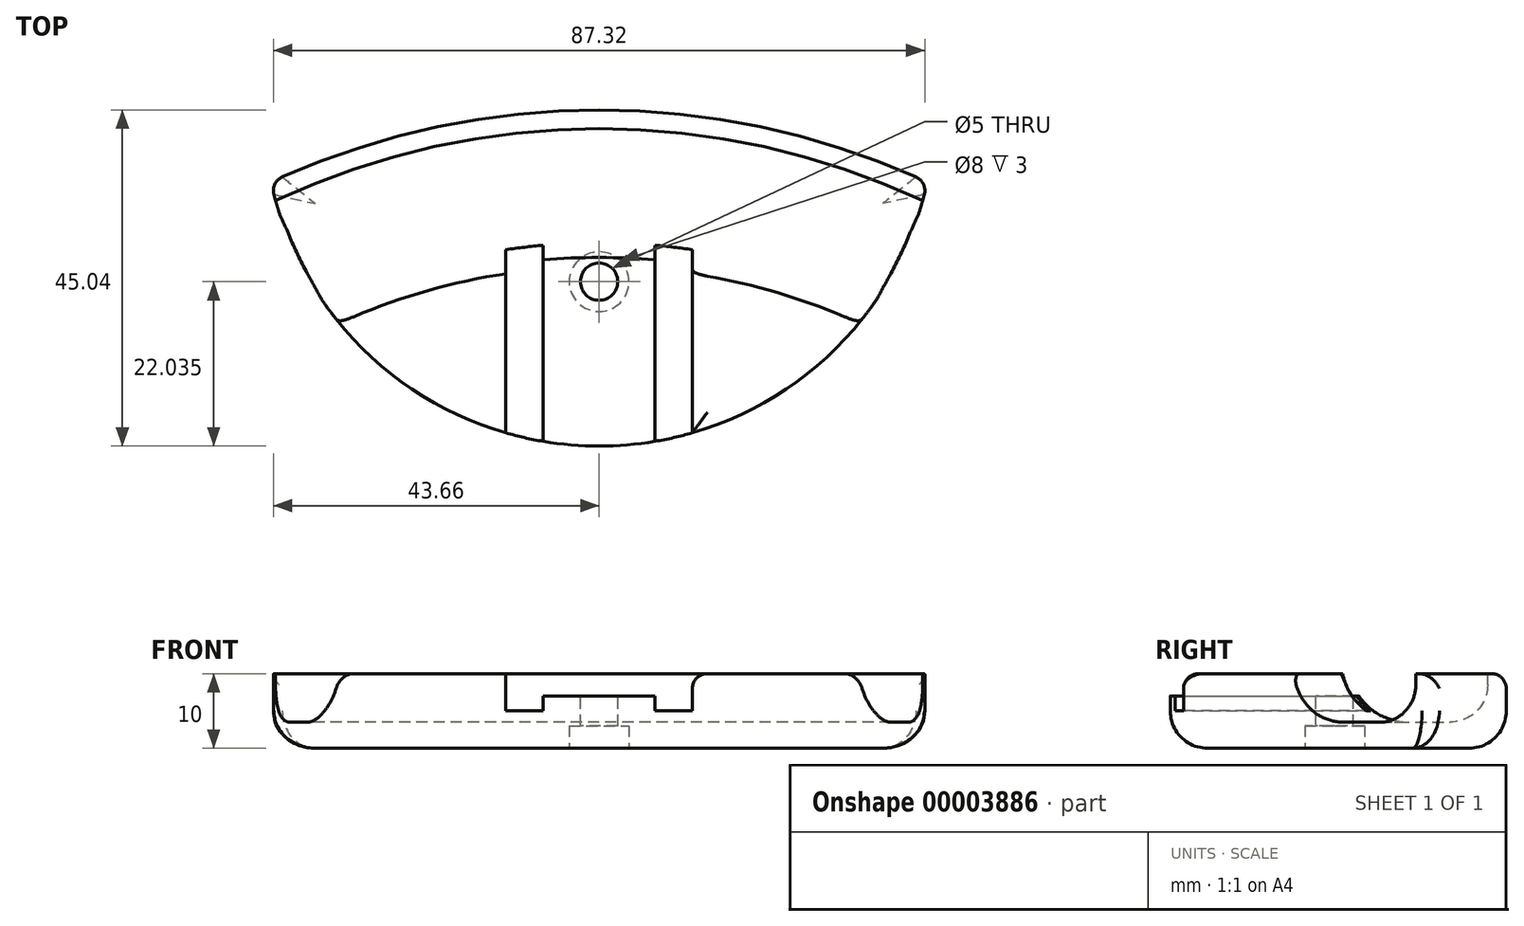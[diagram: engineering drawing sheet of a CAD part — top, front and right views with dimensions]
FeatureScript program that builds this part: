
annotation { "Feature Type Name" : "Feature", "Feature Type Description" : "" }
export const myFeature = defineFeature(function(context is Context, id is Id, definition is map)
    precondition{}
    {
        {
            var Q0;
            Q0=qCreatedBy(makeId("Top.planeOp"),FACE);
            var sketch = newSketch(context, id + "F0", { "sketchPlane" : qUnion([Q0])});
            skLineSegment(sketch, "E0.bottom", {"start": v(-12.5, 20) * mm, "end": v(12.5, 20) * mm});
            skLineSegment(sketch, "E0.top", {"start": v(-12.5, -20) * mm, "end": v(12.5, -20) * mm});
            skLineSegment(sketch, "E0.left", {"start": v(-12.5, 20) * mm, "end": v(-12.5, -20) * mm});
            skLineSegment(sketch, "E0.right", {"start": v(12.5, 20) * mm, "end": v(12.5, -20) * mm});
            skArc(sketch, "E1", {"start": v(43.99, 13.6) * mm, "mid": v(0, 23.27) * mm, "end": v(-43.99, 13.6) * mm});
            skArc(sketch, "E2", {"start": v(-43.99, 13.6) * mm, "mid": v(0, -21.77) * mm, "end": v(43.99, 13.6) * mm});
            skPoint(sketch, "E3", {"position": v(-43.99, 13.6) * mm});
            skPoint(sketch, "E4", {"position": v(43.99, 13.6) * mm});
            skPoint(sketch, "E5", {"position": v(-43.37, 11.14) * mm});
            skPoint(sketch, "E6", {"position": v(43.37, 11.14) * mm});
            skArc(sketch, "E7.trimOffspring", {"start": v(43.37, 11.14) * mm, "mid": v(0, 20.77) * mm, "end": v(-43.37, 11.14) * mm});
            skLineSegment(sketch, "E8", {"start": v(0, 20) * mm, "end": v(0, -20) * mm, "construction": true});
            skArc(sketch, "E9", {"start": v(34.82, -5.3) * mm, "mid": v(0, 2.27) * mm, "end": v(-34.82, -5.3) * mm});
            skPoint(sketch, "E10", {"position": v(0, 0.27) * mm});
            skCircle(sketch, "E11", {"center": v(0, 0.27) * mm, "radius": 2.5 * mm});
            skLineSegment(sketch, "E12", {"start": v(-7.5, -12.17) * mm, "end": v(7.5, -12.17) * mm, "construction": true});
            skPoint(sketch, "E13", {"position": v(0, -12.17) * mm});
            skLineSegment(sketch, "E14", {"start": v(-7.5, -21.14) * mm, "end": v(-7.5, 10.15) * mm});
            skLineSegment(sketch, "E15", {"start": v(7.5, -21.14) * mm, "end": v(7.5, 10.15) * mm});
            skLineSegment(sketch, "E16", {"start": v(-7.5, 10.15) * mm, "end": v(7.5, 10.15) * mm});
            skSolve(sketch);
        }
        {
            var Q0;
            Q0=makeQuery(id+"F0.imprint","IMPRINT",FACE,{"disambiguationData":[TD([[makeQuery(id+"F0.imprint","IMPRINT",EDGE,{"derivedFrom":sQuery(id+"F0.wireOp",EDGE,"E1")}),1.0]])]});
            var Q1;
            {var subQ1=sQuery(id+"F0.wireOp",EDGE,"E7.trimOffspring");Q1=makeQuery(id+"F0.imprint","IMPRINT",FACE,{"disambiguationData":[TD([[makeQuery(id+"F0.imprint","IMPRINT",EDGE,{"derivedFrom":subQ1}),1.0]])]});}
            var Q2;
            {var subQ0=sQuery(id+"F0.wireOp",EDGE,"E9");Q2=makeQuery(id+"F0.imprint","IMPRINT",FACE,{"disambiguationData":[TD([[makeQuery(id+"F0.imprint","IMPRINT",EDGE,{"derivedFrom":subQ0}),1.0]])]});}
            var Q3;
            {var subQ5=sQuery(id+"F0.wireOp",EDGE,"E0.top");Q3=makeQuery(id+"F0.imprint","IMPRINT",FACE,{"disambiguationData":[TD([[makeQuery(id+"F0.imprint","IMPRINT",EDGE,{"derivedFrom":subQ5}),1.0]])]});}
            var Q4;
            {var subQ1=sQuery(id+"F0.wireOp",EDGE,"E0.top");Q4=makeQuery(id+"F0.imprint","IMPRINT",FACE,{"disambiguationData":[TD([[makeQuery(id+"F0.imprint","IMPRINT",EDGE,{"derivedFrom":subQ1}),-1.0]])]});}
            var Q5;
            {var subQ3=sQuery(id+"F0.wireOp",EDGE,"E2");var subQ5=sQuery(id+"F0.wireOp",EDGE,"E7.trimOffspring");var subQ6=makeQuery(id+"F0.imprint","INTERSECT",VERTEX,{"disambiguationData":[OD(0.0)],"derivedFrom":[subQ3,subQ5]});Q5=makeQuery(id+"F0.imprint","IMPRINT",FACE,{"disambiguationData":[TD([[makeQuery(id+"F0.imprint","IMPRINT",EDGE,{"disambiguationData":[TD([[subQ6,1.0]])],"derivedFrom":subQ3}),1.0]])]});}
            var Q6;
            {var subQ5=sQuery(id+"F0.wireOp",EDGE,"E0.bottom");Q6=makeQuery(id+"F0.imprint","IMPRINT",FACE,{"disambiguationData":[TD([[makeQuery(id+"F0.imprint","IMPRINT",EDGE,{"derivedFrom":subQ5}),-1.0]])]});}
            var Q7;
            {var subQ3=sQuery(id+"F0.wireOp",EDGE,"E2");var subQ5=sQuery(id+"F0.wireOp",EDGE,"E7.trimOffspring");var subQ6=makeQuery(id+"F0.imprint","INTERSECT",VERTEX,{"disambiguationData":[OD(1.0)],"derivedFrom":[subQ3,subQ5]});Q7=makeQuery(id+"F0.imprint","IMPRINT",FACE,{"disambiguationData":[TD([[makeQuery(id+"F0.imprint","IMPRINT",EDGE,{"disambiguationData":[TD([[subQ6,-1.0]])],"derivedFrom":subQ3}),1.0]])]});}
            var Q8;
            {var subQ0=sQuery(id+"F0.wireOp",EDGE,"E11");var subQ1=sQuery(id+"F0.wireOp",EDGE,"E9");var subQ3=makeQuery(id+"F0.imprint","INTERSECT",VERTEX,{"disambiguationData":[OD(0.0)],"derivedFrom":[subQ1,subQ0]});Q8=makeQuery(id+"F0.imprint","IMPRINT",FACE,{"disambiguationData":[TD([[makeQuery(id+"F0.imprint","IMPRINT",EDGE,{"disambiguationData":[TD([[subQ3,-1.0]])],"derivedFrom":subQ1}),-1.0]])]});}
            var Q9;
            {var subQ0=sQuery(id+"F0.wireOp",EDGE,"E11");var subQ1=sQuery(id+"F0.wireOp",EDGE,"E9");var subQ3=makeQuery(id+"F0.imprint","INTERSECT",VERTEX,{"disambiguationData":[OD(0.0)],"derivedFrom":[subQ1,subQ0]});Q9=makeQuery(id+"F0.imprint","IMPRINT",FACE,{"disambiguationData":[TD([[makeQuery(id+"F0.imprint","IMPRINT",EDGE,{"disambiguationData":[TD([[subQ3,-1.0]])],"derivedFrom":subQ1}),1.0]])]});}
            var Q10;
            {var subQ0=sQuery(id+"F0.wireOp",EDGE,"E9");var subQ3=sQuery(id+"F0.wireOp",EDGE,"E2");var subQ4=makeQuery(id+"F0.imprint","INTERSECT",VERTEX,{"disambiguationData":[OD(1.0)],"derivedFrom":[subQ3,subQ0]});Q10=makeQuery(id+"F0.imprint","IMPRINT",FACE,{"disambiguationData":[TD([[makeQuery(id+"F0.imprint","IMPRINT",EDGE,{"disambiguationData":[TD([[subQ4,1.0]])],"derivedFrom":subQ0}),1.0]])]});}
            var Q11;
            {var subQ0=sQuery(id+"F0.wireOp",EDGE,"E9");var subQ3=sQuery(id+"F0.wireOp",EDGE,"E2");var subQ4=makeQuery(id+"F0.imprint","INTERSECT",VERTEX,{"disambiguationData":[OD(0.0)],"derivedFrom":[subQ3,subQ0]});Q11=makeQuery(id+"F0.imprint","IMPRINT",FACE,{"disambiguationData":[TD([[makeQuery(id+"F0.imprint","IMPRINT",EDGE,{"disambiguationData":[TD([[subQ4,-1.0]])],"derivedFrom":subQ0}),1.0]])]});}
            var Q12;
            {var subQ4=sQuery(id+"F0.wireOp",EDGE,"f2ed5ddf-1e71-4b46-be9b-5d21263913f5.bottom");Q12=makeQuery(id+"F0.imprint","IMPRINT",FACE,{"disambiguationData":[TD([[makeQuery(id+"F0.imprint","IMPRINT",EDGE,{"derivedFrom":subQ4}),-1.0]])]});}
            var Q13;
            {var subQ0=sQuery(id+"F0.wireOp",EDGE,"f2ed5ddf-1e71-4b46-be9b-5d21263913f5.top");Q13=makeQuery(id+"F0.imprint","IMPRINT",FACE,{"disambiguationData":[TD([[makeQuery(id+"F0.imprint","IMPRINT",EDGE,{"derivedFrom":subQ0}),1.0]])]});}
            var Q14;
            {var subQ1=sQuery(id+"F0.wireOp",EDGE,"E0.bottom");var subQ5=sQuery(id+"F0.wireOp",EDGE,"E14");var subQ6=makeQuery(id+"F0.imprint","INTERSECT",VERTEX,{"derivedFrom":[subQ1,subQ5]});Q14=makeQuery(id+"F0.imprint","IMPRINT",FACE,{"disambiguationData":[TD([[makeQuery(id+"F0.imprint","IMPRINT",EDGE,{"disambiguationData":[TD([[subQ6,-1.0]])],"derivedFrom":subQ1}),1.0]])]});}
            var Q15;
            {var subQ3=sQuery(id+"F0.wireOp",EDGE,"E0.bottom");var subQ8=sQuery(id+"F0.wireOp",EDGE,"E14");var subQ10=makeQuery(id+"F0.imprint","INTERSECT",VERTEX,{"derivedFrom":[subQ3,subQ8]});Q15=makeQuery(id+"F0.imprint","IMPRINT",FACE,{"disambiguationData":[TD([[makeQuery(id+"F0.imprint","IMPRINT",EDGE,{"disambiguationData":[TD([[subQ10,-1.0]])],"derivedFrom":subQ3}),-1.0]])]});}
            var Q16;
            {var subQ3=sQuery(id+"F0.wireOp",EDGE,"E0.top");var subQ5=sQuery(id+"F0.wireOp",EDGE,"E14");var subQ7=makeQuery(id+"F0.imprint","INTERSECT",VERTEX,{"derivedFrom":[subQ3,subQ5]});Q16=makeQuery(id+"F0.imprint","IMPRINT",FACE,{"disambiguationData":[TD([[makeQuery(id+"F0.imprint","IMPRINT",EDGE,{"disambiguationData":[TD([[subQ7,-1.0]])],"derivedFrom":subQ3}),1.0]])]});}
            var Q17;
            {var subQ0=sQuery(id+"F0.wireOp",EDGE,"E14");var subQ1=sQuery(id+"F0.wireOp",EDGE,"E0.top");var subQ2=makeQuery(id+"F0.imprint","INTERSECT",VERTEX,{"derivedFrom":[subQ1,subQ0]});Q17=makeQuery(id+"F0.imprint","IMPRINT",FACE,{"disambiguationData":[TD([[makeQuery(id+"F0.imprint","IMPRINT",EDGE,{"disambiguationData":[TD([[subQ2,-1.0]])],"derivedFrom":subQ1}),-1.0]])]});}
            var Q18;
            {var subQ3=sQuery(id+"F0.wireOp",EDGE,"E16");Q18=makeQuery(id+"F0.imprint","IMPRINT",FACE,{"disambiguationData":[TD([[makeQuery(id+"F0.imprint","IMPRINT",EDGE,{"derivedFrom":subQ3}),-1.0]])]});}
            extrude(context, id + "F1", {"entities" : qUnion([Q0, Q1, Q2, Q3, Q4, Q5, Q6, Q7, Q8, Q9, Q10, Q11, Q12, Q13, Q14, Q15, Q16, Q17, Q18]), "oppositeDirection" : true, "depth" : 10 * mm});
        }
        {
            var Q0;
            {var subQ1=sQuery(id+"F0.wireOp",EDGE,"E7.trimOffspring");Q0=makeQuery(id+"F0.imprint","IMPRINT",FACE,{"disambiguationData":[TD([[makeQuery(id+"F0.imprint","IMPRINT",EDGE,{"derivedFrom":subQ1}),1.0]])]});}
            var Q1;
            {var subQ3=sQuery(id+"F0.wireOp",EDGE,"E2");var subQ5=sQuery(id+"F0.wireOp",EDGE,"E7.trimOffspring");var subQ6=makeQuery(id+"F0.imprint","INTERSECT",VERTEX,{"disambiguationData":[OD(0.0)],"derivedFrom":[subQ3,subQ5]});Q1=makeQuery(id+"F0.imprint","IMPRINT",FACE,{"disambiguationData":[TD([[makeQuery(id+"F0.imprint","IMPRINT",EDGE,{"disambiguationData":[TD([[subQ6,1.0]])],"derivedFrom":subQ3}),1.0]])]});}
            var Q2;
            {var subQ5=sQuery(id+"F0.wireOp",EDGE,"E0.bottom");Q2=makeQuery(id+"F0.imprint","IMPRINT",FACE,{"disambiguationData":[TD([[makeQuery(id+"F0.imprint","IMPRINT",EDGE,{"derivedFrom":subQ5}),-1.0]])]});}
            var Q3;
            {var subQ3=sQuery(id+"F0.wireOp",EDGE,"E2");var subQ5=sQuery(id+"F0.wireOp",EDGE,"E7.trimOffspring");var subQ6=makeQuery(id+"F0.imprint","INTERSECT",VERTEX,{"disambiguationData":[OD(1.0)],"derivedFrom":[subQ3,subQ5]});Q3=makeQuery(id+"F0.imprint","IMPRINT",FACE,{"disambiguationData":[TD([[makeQuery(id+"F0.imprint","IMPRINT",EDGE,{"disambiguationData":[TD([[subQ6,-1.0]])],"derivedFrom":subQ3}),1.0]])]});}
            var Q4;
            {var subQ4=sQuery(id+"F0.wireOp",EDGE,"f2ed5ddf-1e71-4b46-be9b-5d21263913f5.bottom");Q4=makeQuery(id+"F0.imprint","IMPRINT",FACE,{"disambiguationData":[TD([[makeQuery(id+"F0.imprint","IMPRINT",EDGE,{"derivedFrom":subQ4}),-1.0]])]});}
            var Q5;
            {var subQ0=sQuery(id+"F0.wireOp",EDGE,"E11");var subQ1=sQuery(id+"F0.wireOp",EDGE,"E9");var subQ3=makeQuery(id+"F0.imprint","INTERSECT",VERTEX,{"disambiguationData":[OD(0.0)],"derivedFrom":[subQ1,subQ0]});Q5=makeQuery(id+"F0.imprint","IMPRINT",FACE,{"disambiguationData":[TD([[makeQuery(id+"F0.imprint","IMPRINT",EDGE,{"disambiguationData":[TD([[subQ3,-1.0]])],"derivedFrom":subQ1}),-1.0]])]});}
            var Q6;
            {var subQ3=sQuery(id+"F0.wireOp",EDGE,"E0.bottom");var subQ8=sQuery(id+"F0.wireOp",EDGE,"E14");var subQ10=makeQuery(id+"F0.imprint","INTERSECT",VERTEX,{"derivedFrom":[subQ3,subQ8]});Q6=makeQuery(id+"F0.imprint","IMPRINT",FACE,{"disambiguationData":[TD([[makeQuery(id+"F0.imprint","IMPRINT",EDGE,{"disambiguationData":[TD([[subQ10,-1.0]])],"derivedFrom":subQ3}),-1.0]])]});}
            var Q7;
            {var subQ3=sQuery(id+"F0.wireOp",EDGE,"E16");Q7=makeQuery(id+"F0.imprint","IMPRINT",FACE,{"disambiguationData":[TD([[makeQuery(id+"F0.imprint","IMPRINT",EDGE,{"derivedFrom":subQ3}),-1.0]])]});}
            extrude(context, id + "F2", {"entities" : qUnion([Q0, Q1, Q2, Q3, Q4, Q5, Q6, Q7]), "operationType" : NewBodyOperationType.REMOVE, "oppositeDirection" : true, "depth" : 6.5 * mm});
        }
        {
            var Q0;
            {var subQ5=sQuery(id+"F0.wireOp",EDGE,"E0.top");Q0=makeQuery(id+"F0.imprint","IMPRINT",FACE,{"disambiguationData":[TD([[makeQuery(id+"F0.imprint","IMPRINT",EDGE,{"derivedFrom":subQ5}),1.0]])]});}
            var Q1;
            {var subQ1=sQuery(id+"F0.wireOp",EDGE,"E0.top");Q1=makeQuery(id+"F0.imprint","IMPRINT",FACE,{"disambiguationData":[TD([[makeQuery(id+"F0.imprint","IMPRINT",EDGE,{"derivedFrom":subQ1}),-1.0]])]});}
            var Q2;
            {var subQ0=sQuery(id+"F0.wireOp",EDGE,"f2ed5ddf-1e71-4b46-be9b-5d21263913f5.top");Q2=makeQuery(id+"F0.imprint","IMPRINT",FACE,{"disambiguationData":[TD([[makeQuery(id+"F0.imprint","IMPRINT",EDGE,{"derivedFrom":subQ0}),1.0]])]});}
            var Q3;
            {var subQ0=sQuery(id+"F0.wireOp",EDGE,"E11");var subQ1=sQuery(id+"F0.wireOp",EDGE,"E9");var subQ3=makeQuery(id+"F0.imprint","INTERSECT",VERTEX,{"disambiguationData":[OD(0.0)],"derivedFrom":[subQ1,subQ0]});Q3=makeQuery(id+"F0.imprint","IMPRINT",FACE,{"disambiguationData":[TD([[makeQuery(id+"F0.imprint","IMPRINT",EDGE,{"disambiguationData":[TD([[subQ3,-1.0]])],"derivedFrom":subQ1}),1.0]])]});}
            extrude(context, id + "F3", {"entities" : qUnion([Q0, Q1, Q2, Q3]), "operationType" : NewBodyOperationType.REMOVE, "oppositeDirection" : true, "depth" : 5 * mm});
        }
        {
            var Q0;
            {var subQ0=sQuery(id+"F0.wireOp",EDGE,"E9");var subQ1=sQuery(id+"F0.wireOp",EDGE,"E0.right");Q0=makeQuery(id+"F3.boolean.opBoolean","SPLIT",EDGE,{"disambiguationData":[TD([makeQuery(id+"F3.opExtrude","SWEPT_FACE",FACE,{"disambiguationData":[OSD([subQ1])]})])],"derivedFrom":makeQuery(id+"F2.boolean.opBoolean","COPY",EDGE,{"derivedFrom":makeQuery(id+"F2.opExtrude","CAP_EDGE",EDGE,{"disambiguationData":[OSD([subQ0])],"isStart":false})})});}
            var Q1;
            {var subQ0=sQuery(id+"F0.wireOp",EDGE,"E9");var subQ2=sQuery(id+"F0.wireOp",EDGE,"E0.left");Q1=makeQuery(id+"F3.boolean.opBoolean","SPLIT",EDGE,{"disambiguationData":[TD([makeQuery(id+"F3.opExtrude","SWEPT_FACE",FACE,{"disambiguationData":[OSD([subQ2])]})])],"derivedFrom":makeQuery(id+"F2.boolean.opBoolean","COPY",EDGE,{"derivedFrom":makeQuery(id+"F2.opExtrude","CAP_EDGE",EDGE,{"disambiguationData":[OSD([subQ0])],"isStart":false})})});}
            fillet(context, id + "F4", {"entities" : qUnion([Q0, Q1]), "radius" : 8 * mm, "tangentPropagation" : true, "allowEdgeOverflow" : false});
        }
        {
            var Q0;
            Q0=makeQuery(id+"F1.opExtrude","CAP_EDGE",EDGE,{"disambiguationData":[OSD([sQuery(id+"F0.wireOp",EDGE,"E2")])],"isStart":false});
            var Q1;
            Q1=makeQuery(id+"F1.opExtrude","CAP_EDGE",EDGE,{"disambiguationData":[OSD([sQuery(id+"F0.wireOp",EDGE,"E1")])],"isStart":false});
            fillet(context, id + "F5", {"entities" : qUnion([Q0, Q1]), "radius" : 5 * mm, "tangentPropagation" : true, "allowEdgeOverflow" : false});
        }
        {
            var Q0;
            Q0=makeQuery(id+"F1.opExtrude","CAP_EDGE",EDGE,{"disambiguationData":[OSD([sQuery(id+"F0.wireOp",EDGE,"E1")])],"isStart":true});
            var Q1;
            {var subQ0=sQuery(id+"F0.wireOp",EDGE,"E2");var subQ1=makeQuery(id+"F2.opExtrude","SWEPT_FACE",FACE,{"disambiguationData":[OSD([sQuery(id+"F0.wireOp",EDGE,"E9")])]});var subQ2=makeQuery(id+"F1.opExtrude","SWEPT_FACE",FACE,{"disambiguationData":[OSD([subQ0])]});var subQ3=makeQuery(id+"F1.opExtrude","CAP_FACE",FACE,{"disambiguationData":[OSD([sQuery(id+"F0.wireOp",EDGE,"E1"),subQ0])],"isStart":true});Q1=makeQuery(id+"F3.boolean.opBoolean","SPLIT",EDGE,{"disambiguationData":[TD([makeQuery(id+"F3.opExtrude","SWEPT_FACE",FACE,{"disambiguationData":[OSD([sQuery(id+"F0.wireOp",EDGE,"E0.left")])]})])],"derivedFrom":makeQuery(id+"F2.boolean.opBoolean","SPLIT",EDGE,{"disambiguationData":[TD([subQ3,subQ2,subQ1])],"derivedFrom":makeQuery(id+"F1.opExtrude","CAP_EDGE",EDGE,{"disambiguationData":[OSD([subQ0])],"isStart":true})})});}
            var Q2;
            {var subQ0=sQuery(id+"F0.wireOp",EDGE,"E2");var subQ1=makeQuery(id+"F2.opExtrude","SWEPT_FACE",FACE,{"disambiguationData":[OSD([sQuery(id+"F0.wireOp",EDGE,"E9")])]});var subQ2=makeQuery(id+"F1.opExtrude","SWEPT_FACE",FACE,{"disambiguationData":[OSD([subQ0])]});var subQ3=makeQuery(id+"F1.opExtrude","CAP_FACE",FACE,{"disambiguationData":[OSD([sQuery(id+"F0.wireOp",EDGE,"E1"),subQ0])],"isStart":true});Q2=makeQuery(id+"F3.boolean.opBoolean","SPLIT",EDGE,{"disambiguationData":[TD([makeQuery(id+"F3.opExtrude","SWEPT_FACE",FACE,{"disambiguationData":[OSD([sQuery(id+"F0.wireOp",EDGE,"E0.right")])]})])],"derivedFrom":makeQuery(id+"F2.boolean.opBoolean","SPLIT",EDGE,{"disambiguationData":[TD([subQ3,subQ2,subQ1])],"derivedFrom":makeQuery(id+"F1.opExtrude","CAP_EDGE",EDGE,{"disambiguationData":[OSD([subQ0])],"isStart":true})})});}
            var Q3;
            Q3=makeQuery(id+"F3.boolean.opBoolean","COPY",EDGE,{"derivedFrom":makeQuery(id+"F3.opExtrude","SWEPT_EDGE",EDGE,{"disambiguationData":[OSD([sQuery(id+"F0.wireOp",EDGE,"E0.top"),sQuery(id+"F0.wireOp",EDGE,"E0.right"),sQuery(id+"F0.wireOp",EDGE,"E2")])]})});
            var Q4;
            Q4=makeQuery(id+"F3.boolean.opBoolean","COPY",EDGE,{"derivedFrom":makeQuery(id+"F3.opExtrude","SWEPT_EDGE",EDGE,{"disambiguationData":[OSD([sQuery(id+"F0.wireOp",EDGE,"E0.top"),sQuery(id+"F0.wireOp",EDGE,"E0.left"),sQuery(id+"F0.wireOp",EDGE,"E2")])]})});
            var Q5;
            Q5=makeQuery(id+"F3.boolean.opBoolean","COPY",EDGE,{"derivedFrom":makeQuery(id+"F3.opExtrude","CAP_EDGE",EDGE,{"disambiguationData":[OSD([sQuery(id+"F0.wireOp",EDGE,"E0.left")])],"isStart":true})});
            var Q6;
            Q6=makeQuery(id+"F3.boolean.opBoolean","COPY",EDGE,{"derivedFrom":makeQuery(id+"F3.opExtrude","CAP_EDGE",EDGE,{"disambiguationData":[OSD([sQuery(id+"F0.wireOp",EDGE,"E0.right")])],"isStart":true})});
            var Q7;
            {var subQ0=sQuery(id+"F0.wireOp",EDGE,"E9");Q7=makeQuery(id+"F3.boolean.opBoolean","SPLIT",EDGE,{"disambiguationData":[TD([makeQuery(id+"F3.opExtrude","SWEPT_FACE",FACE,{"disambiguationData":[OSD([sQuery(id+"F0.wireOp",EDGE,"E0.left")])]})])],"derivedFrom":makeQuery(id+"F2.boolean.opBoolean","COPY",EDGE,{"derivedFrom":makeQuery(id+"F2.opExtrude","CAP_EDGE",EDGE,{"disambiguationData":[OSD([subQ0])],"isStart":true})})});}
            var Q8;
            {var subQ0=sQuery(id+"F0.wireOp",EDGE,"E9");Q8=makeQuery(id+"F3.boolean.opBoolean","SPLIT",EDGE,{"disambiguationData":[TD([makeQuery(id+"F3.opExtrude","SWEPT_FACE",FACE,{"disambiguationData":[OSD([sQuery(id+"F0.wireOp",EDGE,"E0.right")])]})])],"derivedFrom":makeQuery(id+"F2.boolean.opBoolean","COPY",EDGE,{"derivedFrom":makeQuery(id+"F2.opExtrude","CAP_EDGE",EDGE,{"disambiguationData":[OSD([subQ0])],"isStart":true})})});}
            var Q9;
            Q9=makeQuery(id+"F2.boolean.opBoolean","COPY",EDGE,{"derivedFrom":makeQuery(id+"F2.opExtrude","CAP_EDGE",EDGE,{"disambiguationData":[OSD([sQuery(id+"F0.wireOp",EDGE,"E7.trimOffspring")])],"isStart":true})});
            var Q10;
            {var subQ0=sQuery(id+"F0.wireOp",EDGE,"E1");var subQ1=sQuery(id+"F0.wireOp",EDGE,"E2");Q10=makeQuery(id+"F1.opExtrude","SWEPT_EDGE",EDGE,{"disambiguationData":[OSD([subQ0,subQ1]),TDD([makeQuery(id+"F0.imprint","INTERSECT",VERTEX,{"disambiguationData":[OD(1.0)],"derivedFrom":[subQ0,subQ1]})])]});}
            var Q11;
            {var subQ0=sQuery(id+"F0.wireOp",EDGE,"E1");var subQ1=sQuery(id+"F0.wireOp",EDGE,"E2");Q11=makeQuery(id+"F1.opExtrude","SWEPT_EDGE",EDGE,{"disambiguationData":[OSD([subQ0,subQ1]),TDD([makeQuery(id+"F0.imprint","INTERSECT",VERTEX,{"disambiguationData":[OD(0.0)],"derivedFrom":[subQ0,subQ1]})])]});}
            fillet(context, id + "F6", {"entities" : qUnion([Q0, Q1, Q2, Q3, Q4, Q5, Q6, Q7, Q8, Q9, Q10, Q11]), "radius" : 2 * mm, "tangentPropagation" : true, "allowEdgeOverflow" : false});
        }
        {
            var Q0;
            Q0=makeQuery(id+"F2.boolean.opBoolean","COPY",EDGE,{"derivedFrom":makeQuery(id+"F2.opExtrude","CAP_EDGE",EDGE,{"disambiguationData":[OSD([sQuery(id+"F0.wireOp",EDGE,"E7.trimOffspring")])],"isStart":false})});
            fillet(context, id + "F7", {"entities" : qUnion([Q0]), "radius" : 5 * mm, "tangentPropagation" : true, "allowEdgeOverflow" : false});
        }
        {
            var Q0;
            {var subQ0=sQuery(id+"F0.wireOp",EDGE,"E11");var subQ1=sQuery(id+"F0.wireOp",EDGE,"E9");var subQ3=makeQuery(id+"F0.imprint","INTERSECT",VERTEX,{"disambiguationData":[OD(0.0)],"derivedFrom":[subQ1,subQ0]});Q0=makeQuery(id+"F0.imprint","IMPRINT",FACE,{"disambiguationData":[TD([[makeQuery(id+"F0.imprint","IMPRINT",EDGE,{"disambiguationData":[TD([[subQ3,-1.0]])],"derivedFrom":subQ1}),-1.0]])]});}
            var Q1;
            {var subQ0=sQuery(id+"F0.wireOp",EDGE,"E11");var subQ1=sQuery(id+"F0.wireOp",EDGE,"E9");var subQ3=makeQuery(id+"F0.imprint","INTERSECT",VERTEX,{"disambiguationData":[OD(0.0)],"derivedFrom":[subQ1,subQ0]});Q1=makeQuery(id+"F0.imprint","IMPRINT",FACE,{"disambiguationData":[TD([[makeQuery(id+"F0.imprint","IMPRINT",EDGE,{"disambiguationData":[TD([[subQ3,-1.0]])],"derivedFrom":subQ1}),1.0]])]});}
            extrude(context, id + "F8", {"entities" : qUnion([Q0, Q1]), "operationType" : NewBodyOperationType.REMOVE, "endBound" : BoundingType.THROUGH_ALL, "oppositeDirection" : true, "depth" : 20 * mm});
        }
        {
            var Q0;
            Q0=makeQuery(id+"F1.opExtrude","CAP_FACE",FACE,{"disambiguationData":[OSD([sQuery(id+"F0.wireOp",EDGE,"E1"),sQuery(id+"F0.wireOp",EDGE,"E2")])],"isStart":false});
            var sketch = newSketch(context, id + "F9", { "sketchPlane" : qUnion([Q0])});
            skCircle(sketch, "E17", {"center": v(0, -0.27) * mm, "radius": 4 * mm});
            skSolve(sketch);
        }
        {
            var Q0;
            Q0=makeQuery(id+"F9.imprint","IMPRINT",FACE,{"disambiguationData":[TD([[makeQuery(id+"F9.imprint","IMPRINT",EDGE,{"derivedFrom":makeQuery(id+"F8.boolean.opBoolean","INTERSECT",EDGE,{"derivedFrom":[makeQuery(id+"F1.opExtrude","CAP_FACE",FACE,{"disambiguationData":[OSD([sQuery(id+"F0.wireOp",EDGE,"E1"),sQuery(id+"F0.wireOp",EDGE,"E2")])],"isStart":false}),makeQuery(id+"F8.opExtrude","SWEPT_FACE",FACE,{"disambiguationData":[OSD([sQuery(id+"F0.wireOp",EDGE,"E11")])]})]})}),-1.0]])]});
            var Q1;
            Q1=makeQuery(id+"F9.imprint","IMPRINT",FACE,{"disambiguationData":[TD([[makeQuery(id+"F9.imprint","IMPRINT",EDGE,{"derivedFrom":sQuery(id+"F9.wireOp",EDGE,"E17")}),1.0]])]});
            extrude(context, id + "F10", {"entities" : qUnion([Q0, Q1]), "operationType" : NewBodyOperationType.REMOVE, "oppositeDirection" : true, "depth" : 3 * mm});
        }
        {
            var Q0;
            {var subQ3=sQuery(id+"F0.wireOp",EDGE,"E0.top");var subQ5=sQuery(id+"F0.wireOp",EDGE,"E14");var subQ7=makeQuery(id+"F0.imprint","INTERSECT",VERTEX,{"derivedFrom":[subQ3,subQ5]});Q0=makeQuery(id+"F0.imprint","IMPRINT",FACE,{"disambiguationData":[TD([[makeQuery(id+"F0.imprint","IMPRINT",EDGE,{"disambiguationData":[TD([[subQ7,-1.0]])],"derivedFrom":subQ3}),1.0]])]});}
            var Q1;
            {var subQ3=sQuery(id+"F0.wireOp",EDGE,"E16");Q1=makeQuery(id+"F0.imprint","IMPRINT",FACE,{"disambiguationData":[TD([[makeQuery(id+"F0.imprint","IMPRINT",EDGE,{"derivedFrom":subQ3}),-1.0]])]});}
            var Q2;
            {var subQ1=sQuery(id+"F0.wireOp",EDGE,"E0.top");var subQ5=sQuery(id+"F0.wireOp",EDGE,"E14");var subQ6=makeQuery(id+"F0.imprint","INTERSECT",VERTEX,{"derivedFrom":[subQ1,subQ5]});Q2=makeQuery(id+"F0.imprint","IMPRINT",FACE,{"disambiguationData":[TD([[makeQuery(id+"F0.imprint","IMPRINT",EDGE,{"disambiguationData":[TD([[subQ6,-1.0]])],"derivedFrom":subQ1}),-1.0]])]});}
            extrude(context, id + "F11", {"entities" : qUnion([Q0, Q1, Q2]), "operationType" : NewBodyOperationType.REMOVE, "oppositeDirection" : true, "depth" : 3 * mm});
        }
    });
